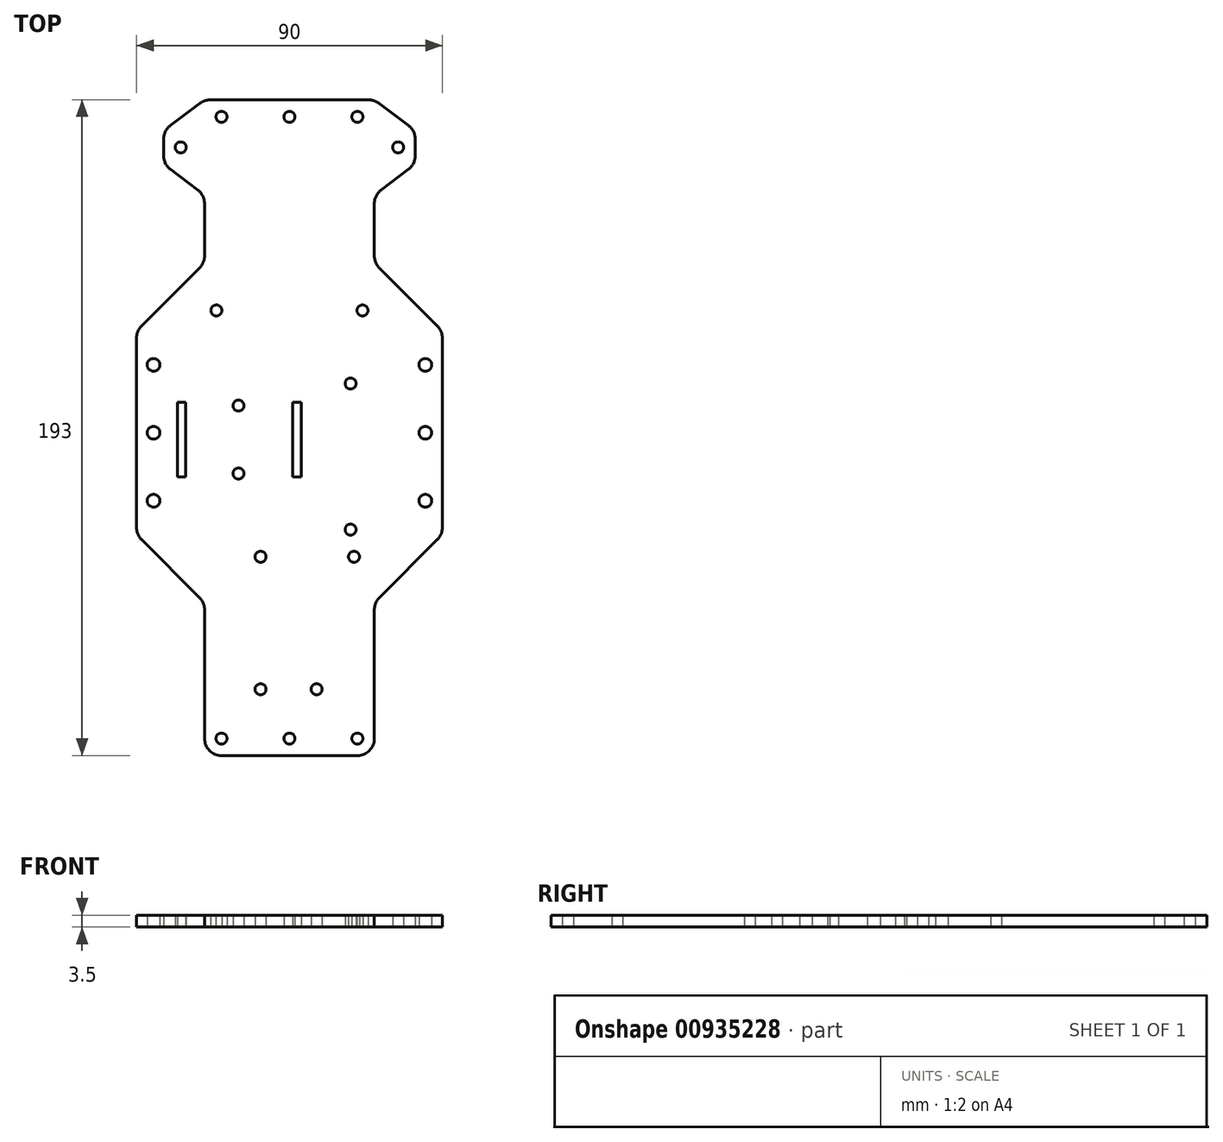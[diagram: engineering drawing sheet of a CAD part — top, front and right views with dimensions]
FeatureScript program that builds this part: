
annotation { "Feature Type Name" : "Feature", "Feature Type Description" : "" }
export const myFeature = defineFeature(function(context is Context, id is Id, definition is map)
    precondition{}
    {
        {
            var Q0;
            Q0=qCreatedBy(makeId("Top.planeOp"),FACE);
            var sketch = newSketch(context, id + "F0", { "sketchPlane" : qUnion([Q0])});
            skPoint(sketch, "E0.middle", {"position": v(0, 0) * mm});
            skLineSegment(sketch, "E1.left", {"start": v(-45, 32) * mm, "end": v(-45, -28) * mm});
            skLineSegment(sketch, "E1.right", {"start": v(45, 32) * mm, "end": v(45, -28) * mm});
            skLineSegment(sketch, "E2.bottom", {"start": v(-25, 100) * mm, "end": v(25, 100) * mm});
            skLineSegment(sketch, "E2.top", {"start": v(-20, -93) * mm, "end": v(20, -93) * mm});
            skLineSegment(sketch, "E2.right", {"start": v(25, 72) * mm, "end": v(25, 52) * mm});
            skLineSegment(sketch, "E3.trimOffspring", {"start": v(-25, -48) * mm, "end": v(-25, -88) * mm});
            skLineSegment(sketch, "E4.trimOffspring", {"start": v(25, -48) * mm, "end": v(25, -88) * mm});
            skLineSegment(sketch, "E5", {"start": v(-25, 100) * mm, "end": v(-37, 91) * mm});
            skLineSegment(sketch, "E6", {"start": v(-37, 91) * mm, "end": v(-37, 81) * mm});
            skLineSegment(sketch, "E7", {"start": v(-37, 81) * mm, "end": v(-25, 72) * mm});
            skLineSegment(sketch, "E8.MirrorCS", {"start": v(37, 81) * mm, "end": v(25, 72) * mm});
            skLineSegment(sketch, "E9.MirrorCS", {"start": v(37, 91) * mm, "end": v(37, 81) * mm});
            skLineSegment(sketch, "E10.MirrorCS", {"start": v(25, 100) * mm, "end": v(37, 91) * mm});
            skCircle(sketch, "E11", {"center": v(-32, 86) * mm, "radius": 1.63 * mm});
            skLineSegment(sketch, "E12", {"start": v(-32, 86) * mm, "end": v(-32, 94.75) * mm, "construction": true});
            skLineSegment(sketch, "E13", {"start": v(-32, 86) * mm, "end": v(-32, 77.25) * mm, "construction": true});
            skLineSegment(sketch, "E14", {"start": v(-45, 32) * mm, "end": v(-25, 52) * mm});
            skLineSegment(sketch, "E15", {"start": v(45, 32) * mm, "end": v(25, 52) * mm});
            skLineSegment(sketch, "E16", {"start": v(-45, -28) * mm, "end": v(-25, -48) * mm});
            skLineSegment(sketch, "E17", {"start": v(45, -28) * mm, "end": v(25, -48) * mm});
            skCircle(sketch, "E18", {"center": v(0, 95) * mm, "radius": 1.63 * mm});
            skCircle(sketch, "E19", {"center": v(-20, 95) * mm, "radius": 1.63 * mm});
            skCircle(sketch, "E20", {"center": v(21.5, 38) * mm, "radius": 1.63 * mm});
            skCircle(sketch, "E21", {"center": v(-21.5, 38) * mm, "radius": 1.63 * mm});
            skPoint(sketch, "E22.visualSharp", {"position": v(25, -93) * mm});
            skArc(sketch, "E22.filletArc", {"start": v(20, -93) * mm, "mid": v(23.54, -91.54) * mm, "end": v(25, -88) * mm});
            skPoint(sketch, "E23.visualSharp", {"position": v(-25, -93) * mm});
            skArc(sketch, "E23.filletArc", {"start": v(-25, -88) * mm, "mid": v(-23.54, -91.54) * mm, "end": v(-20, -93) * mm});
            skLineSegment(sketch, "E24.trimOffspring", {"start": v(-25, 72) * mm, "end": v(-25, 52) * mm});
            skCircle(sketch, "E25", {"center": v(32, 86) * mm, "radius": 1.63 * mm});
            skLineSegment(sketch, "E26", {"start": v(32, 86) * mm, "end": v(32, 94.75) * mm, "construction": true});
            skLineSegment(sketch, "E27", {"start": v(32, 86) * mm, "end": v(32, 77.25) * mm, "construction": true});
            skLineSegment(sketch, "E28", {"start": v(-32, 86) * mm, "end": v(-37, 86) * mm, "construction": true});
            skLineSegment(sketch, "E29", {"start": v(32, 86) * mm, "end": v(37, 86) * mm, "construction": true});
            skCircle(sketch, "E30", {"center": v(20, 95) * mm, "radius": 1.63 * mm});
            skLineSegment(sketch, "E31", {"start": v(0, 95) * mm, "end": v(-20, 95) * mm, "construction": true});
            skLineSegment(sketch, "E32", {"start": v(0, 95) * mm, "end": v(20, 95) * mm, "construction": true});
            skCircle(sketch, "E33", {"center": v(0, -88) * mm, "radius": 1.63 * mm});
            skCircle(sketch, "E34", {"center": v(-20, -88) * mm, "radius": 1.63 * mm});
            skCircle(sketch, "E35", {"center": v(20, -88) * mm, "radius": 1.63 * mm});
            skPoint(sketch, "E36", {"position": v(0, -93) * mm});
            skLineSegment(sketch, "E37", {"start": v(0, -88) * mm, "end": v(-20, -88) * mm, "construction": true});
            skLineSegment(sketch, "E38", {"start": v(0, -88) * mm, "end": v(20, -88) * mm, "construction": true});
            skLineSegment(sketch, "E39", {"start": v(-25, -82) * mm, "end": v(25, -82) * mm, "construction": true});
            skCircle(sketch, "E40", {"center": v(-8.5, -34.5) * mm, "radius": 1.63 * mm});
            skCircle(sketch, "E41.MirrorC", {"center": v(19, -34.5) * mm, "radius": 1.63 * mm});
            skCircle(sketch, "E42", {"center": v(-8.5, -73.5) * mm, "radius": 1.63 * mm});
            skLineSegment(sketch, "E43", {"start": v(0, -30.5) * mm, "end": v(24.04, -30.5) * mm, "construction": true});
            skCircle(sketch, "E44", {"center": v(8, -73.5) * mm, "radius": 1.63 * mm});
            skCircle(sketch, "E45", {"center": v(-40, 22) * mm, "radius": 1.88 * mm});
            skCircle(sketch, "E46", {"center": v(-40, 2) * mm, "radius": 1.88 * mm});
            skCircle(sketch, "E47", {"center": v(-40, -18) * mm, "radius": 1.88 * mm});
            skCircle(sketch, "E48", {"center": v(40, 22) * mm, "radius": 1.88 * mm});
            skCircle(sketch, "E49", {"center": v(40, 2) * mm, "radius": 1.88 * mm});
            skCircle(sketch, "E50", {"center": v(40, -18) * mm, "radius": 1.88 * mm});
            skCircle(sketch, "E51", {"center": v(18, 16.5) * mm, "radius": 1.63 * mm});
            skCircle(sketch, "E52", {"center": v(18, -26.5) * mm, "radius": 1.63 * mm});
            skLineSegment(sketch, "E53.bottom", {"start": v(-33, 11) * mm, "end": v(-30.5, 11) * mm});
            skLineSegment(sketch, "E53.top", {"start": v(-33, -11) * mm, "end": v(-30.5, -11) * mm});
            skLineSegment(sketch, "E53.left", {"start": v(-33, 11) * mm, "end": v(-33, -11) * mm});
            skLineSegment(sketch, "E53.right", {"start": v(-30.5, 11) * mm, "end": v(-30.5, -11) * mm});
            skLineSegment(sketch, "E54.bottom", {"start": v(-30, 27) * mm, "end": v(0, 27) * mm, "construction": true});
            skLineSegment(sketch, "E54.top", {"start": v(-30, -27) * mm, "end": v(0, -27) * mm, "construction": true});
            skLineSegment(sketch, "E54.left", {"start": v(-30, 27) * mm, "end": v(-30, -27) * mm, "construction": true});
            skLineSegment(sketch, "E54.right", {"start": v(0, 27) * mm, "end": v(0, -27) * mm, "construction": true});
            skLineSegment(sketch, "E55.bottom", {"start": v(1, 11) * mm, "end": v(3.5, 11) * mm});
            skLineSegment(sketch, "E55.top", {"start": v(1, -11) * mm, "end": v(3.5, -11) * mm});
            skLineSegment(sketch, "E55.left", {"start": v(1, 11) * mm, "end": v(1, -11) * mm});
            skLineSegment(sketch, "E55.right", {"start": v(3.5, 11) * mm, "end": v(3.5, -11) * mm});
            skLineSegment(sketch, "E56", {"start": v(-21.5, 38) * mm, "end": v(-25, 38) * mm, "construction": true});
            skLineSegment(sketch, "E57", {"start": v(21.5, 38) * mm, "end": v(25, 38) * mm, "construction": true});
            skPoint(sketch, "E58", {"position": v(-45, 2) * mm});
            skCircle(sketch, "E59", {"center": v(-15, 10) * mm, "radius": 1.63 * mm});
            skCircle(sketch, "E60", {"center": v(-15, -10) * mm, "radius": 1.63 * mm});
            skLineSegment(sketch, "E61", {"start": v(-15, 10) * mm, "end": v(-15, 0) * mm, "construction": true});
            skLineSegment(sketch, "E62", {"start": v(-15, 0) * mm, "end": v(-15, -10) * mm, "construction": true});
            skLineSegment(sketch, "E63", {"start": v(-30, 0) * mm, "end": v(-15, 0) * mm, "construction": true});
            skLineSegment(sketch, "E64", {"start": v(0, 0) * mm, "end": v(-15, 0) * mm, "construction": true});
            skSolve(sketch);
        }
        {
            var Q0;
            {var subQ5=sQuery(id+"F0.wireOp",EDGE,"E1.bottom");Q0=makeQuery(id+"F0.imprint","IMPRINT",FACE,{"disambiguationData":[TD([[makeQuery(id+"F0.imprint","IMPRINT",EDGE,{"derivedFrom":subQ5}),-1.0]])]});}
            var Q1;
            {var subQ0=sQuery(id+"F0.wireOp",EDGE,"E1.bottom");Q1=makeQuery(id+"F0.imprint","IMPRINT",FACE,{"disambiguationData":[TD([[makeQuery(id+"F0.imprint","IMPRINT",EDGE,{"derivedFrom":subQ0}),1.0]])]});}
            var Q2;
            {var subQ2=sQuery(id+"F0.wireOp",EDGE,"mY936AxS-bCtM-u6mH-qkgE-3i1a7G4UpAxP");Q2=makeQuery(id+"F0.imprint","IMPRINT",FACE,{"disambiguationData":[TD([[makeQuery(id+"F0.imprint","IMPRINT",EDGE,{"derivedFrom":subQ2}),1.0]])]});}
            var Q3;
            {var subQ0=sQuery(id+"F0.wireOp",EDGE,"tlpUXb4p-dup2-cb7J-fJeQ-cunatJqCv4r3");Q3=makeQuery(id+"F0.imprint","IMPRINT",FACE,{"disambiguationData":[TD([[makeQuery(id+"F0.imprint","IMPRINT",EDGE,{"derivedFrom":subQ0}),-1.0]])]});}
            var Q4;
            {var subQ0=sQuery(id+"F0.wireOp",EDGE,"E1.top");Q4=makeQuery(id+"F0.imprint","IMPRINT",FACE,{"disambiguationData":[TD([[makeQuery(id+"F0.imprint","IMPRINT",EDGE,{"derivedFrom":subQ0}),-1.0]])]});}
            var Q5;
            {var subQ0=sQuery(id+"F0.wireOp",EDGE,"E5");Q5=makeQuery(id+"F0.imprint","IMPRINT",FACE,{"disambiguationData":[TD([[makeQuery(id+"F0.imprint","IMPRINT",EDGE,{"derivedFrom":subQ0}),1.0]])]});}
            var Q6;
            {var subQ0=sQuery(id+"F0.wireOp",EDGE,"pqNEKcwJ-h33T-HL2r-peva-7RRUNKeUBN5d");Q6=makeQuery(id+"F0.imprint","IMPRINT",FACE,{"disambiguationData":[TD([[makeQuery(id+"F0.imprint","IMPRINT",EDGE,{"derivedFrom":subQ0}),-1.0]])]});}
            var Q7;
            {var subQ0=sQuery(id+"F0.wireOp",EDGE,"a00ee1d5-904a-4f26-b629-e24fb3101e3a.trimOffspring");Q7=makeQuery(id+"F0.imprint","IMPRINT",FACE,{"disambiguationData":[TD([[makeQuery(id+"F0.imprint","IMPRINT",EDGE,{"derivedFrom":subQ0}),1.0]])]});}
            var Q8;
            {var subQ0=sQuery(id+"F0.wireOp",EDGE,"a8a4ccb4-9108-42de-b2b3-bf1162c27bd3.trimOffspring");Q8=makeQuery(id+"F0.imprint","IMPRINT",FACE,{"disambiguationData":[TD([[makeQuery(id+"F0.imprint","IMPRINT",EDGE,{"derivedFrom":subQ0}),-1.0]])]});}
            var Q9;
            {var subQ2=sQuery(id+"F0.wireOp",EDGE,"22062ab9-91ba-4eca-898b-d4dce9db847a0.MirrorCS");Q9=makeQuery(id+"F0.imprint","IMPRINT",FACE,{"disambiguationData":[TD([[makeQuery(id+"F0.imprint","IMPRINT",EDGE,{"derivedFrom":subQ2}),1.0]])]});}
            var Q10;
            {var subQ0=sQuery(id+"F0.wireOp",EDGE,"326a62c6-d771-4757-9c2b-3534473035e10.MirrorCS");Q10=makeQuery(id+"F0.imprint","IMPRINT",FACE,{"disambiguationData":[TD([[makeQuery(id+"F0.imprint","IMPRINT",EDGE,{"derivedFrom":subQ0}),-1.0]])]});}
            var Q11;
            {var subQ2=sQuery(id+"F0.wireOp",EDGE,"E8.MirrorCS");Q11=makeQuery(id+"F0.imprint","IMPRINT",FACE,{"disambiguationData":[TD([[makeQuery(id+"F0.imprint","IMPRINT",EDGE,{"derivedFrom":subQ2}),-1.0]])]});}
            extrude(context, id + "F1", {"entities" : qUnion([Q0, Q1, Q2, Q3, Q4, Q5, Q6, Q7, Q8, Q9, Q10, Q11]), "depth" : 3.5 * mm, "offsetDistance" : 25 * mm});
        }
        {
            var Q0;
            Q0=makeQuery(id+"F1.opExtrude","SWEPT_EDGE",EDGE,{"disambiguationData":[OSD([sQuery(id+"F0.wireOp",EDGE,"E1.left"),sQuery(id+"F0.wireOp",EDGE,"E16")])]});
            var Q1;
            Q1=makeQuery(id+"F1.opExtrude","SWEPT_EDGE",EDGE,{"disambiguationData":[OSD([sQuery(id+"F0.wireOp",EDGE,"E3.trimOffspring"),sQuery(id+"F0.wireOp",EDGE,"E16")])]});
            var Q2;
            Q2=makeQuery(id+"F1.opExtrude","SWEPT_EDGE",EDGE,{"disambiguationData":[OSD([sQuery(id+"F0.wireOp",EDGE,"E4.trimOffspring"),sQuery(id+"F0.wireOp",EDGE,"E17")])]});
            var Q3;
            Q3=makeQuery(id+"F1.opExtrude","SWEPT_EDGE",EDGE,{"disambiguationData":[OSD([sQuery(id+"F0.wireOp",EDGE,"E1.right"),sQuery(id+"F0.wireOp",EDGE,"E17")])]});
            var Q4;
            Q4=makeQuery(id+"F1.opExtrude","SWEPT_EDGE",EDGE,{"disambiguationData":[OSD([sQuery(id+"F0.wireOp",EDGE,"E1.right"),sQuery(id+"F0.wireOp",EDGE,"E15")])]});
            var Q5;
            Q5=makeQuery(id+"F1.opExtrude","SWEPT_EDGE",EDGE,{"disambiguationData":[OSD([sQuery(id+"F0.wireOp",EDGE,"E2.right"),sQuery(id+"F0.wireOp",EDGE,"E15")])]});
            var Q6;
            Q6=makeQuery(id+"F1.opExtrude","SWEPT_EDGE",EDGE,{"disambiguationData":[OSD([sQuery(id+"F0.wireOp",EDGE,"E2.right"),sQuery(id+"F0.wireOp",EDGE,"E8.MirrorCS")])]});
            var Q7;
            Q7=makeQuery(id+"F1.opExtrude","SWEPT_EDGE",EDGE,{"disambiguationData":[OSD([sQuery(id+"F0.wireOp",EDGE,"E14"),sQuery(id+"F0.wireOp",EDGE,"E24.trimOffspring")])]});
            var Q8;
            Q8=makeQuery(id+"F1.opExtrude","SWEPT_EDGE",EDGE,{"disambiguationData":[OSD([sQuery(id+"F0.wireOp",EDGE,"E1.left"),sQuery(id+"F0.wireOp",EDGE,"E14")])]});
            var Q9;
            Q9=makeQuery(id+"F1.opExtrude","SWEPT_EDGE",EDGE,{"disambiguationData":[OSD([sQuery(id+"F0.wireOp",EDGE,"E7"),sQuery(id+"F0.wireOp",EDGE,"E24.trimOffspring")])]});
            var Q10;
            Q10=makeQuery(id+"F1.opExtrude","SWEPT_EDGE",EDGE,{"disambiguationData":[OSD([sQuery(id+"F0.wireOp",EDGE,"E6"),sQuery(id+"F0.wireOp",EDGE,"E7")])]});
            var Q11;
            Q11=makeQuery(id+"F1.opExtrude","SWEPT_EDGE",EDGE,{"disambiguationData":[OSD([sQuery(id+"F0.wireOp",EDGE,"E5"),sQuery(id+"F0.wireOp",EDGE,"E6")])]});
            var Q12;
            Q12=makeQuery(id+"F1.opExtrude","SWEPT_EDGE",EDGE,{"disambiguationData":[OSD([sQuery(id+"F0.wireOp",EDGE,"E2.bottom"),sQuery(id+"F0.wireOp",EDGE,"E5")])]});
            var Q13;
            Q13=makeQuery(id+"F1.opExtrude","SWEPT_EDGE",EDGE,{"disambiguationData":[OSD([sQuery(id+"F0.wireOp",EDGE,"E2.bottom"),sQuery(id+"F0.wireOp",EDGE,"E10.MirrorCS")])]});
            var Q14;
            Q14=makeQuery(id+"F1.opExtrude","SWEPT_EDGE",EDGE,{"disambiguationData":[OSD([sQuery(id+"F0.wireOp",EDGE,"E9.MirrorCS"),sQuery(id+"F0.wireOp",EDGE,"E10.MirrorCS")])]});
            var Q15;
            Q15=makeQuery(id+"F1.opExtrude","SWEPT_EDGE",EDGE,{"disambiguationData":[OSD([sQuery(id+"F0.wireOp",EDGE,"E8.MirrorCS"),sQuery(id+"F0.wireOp",EDGE,"E9.MirrorCS")])]});
            fillet(context, id + "F2", {"entities" : qUnion([Q0, Q1, Q2, Q3, Q4, Q5, Q6, Q7, Q8, Q9, Q10, Q11, Q12, Q13, Q14, Q15]), "radius" : 5 * mm, "tangentPropagation" : true, "allowEdgeOverflow" : false});
        }
    });
